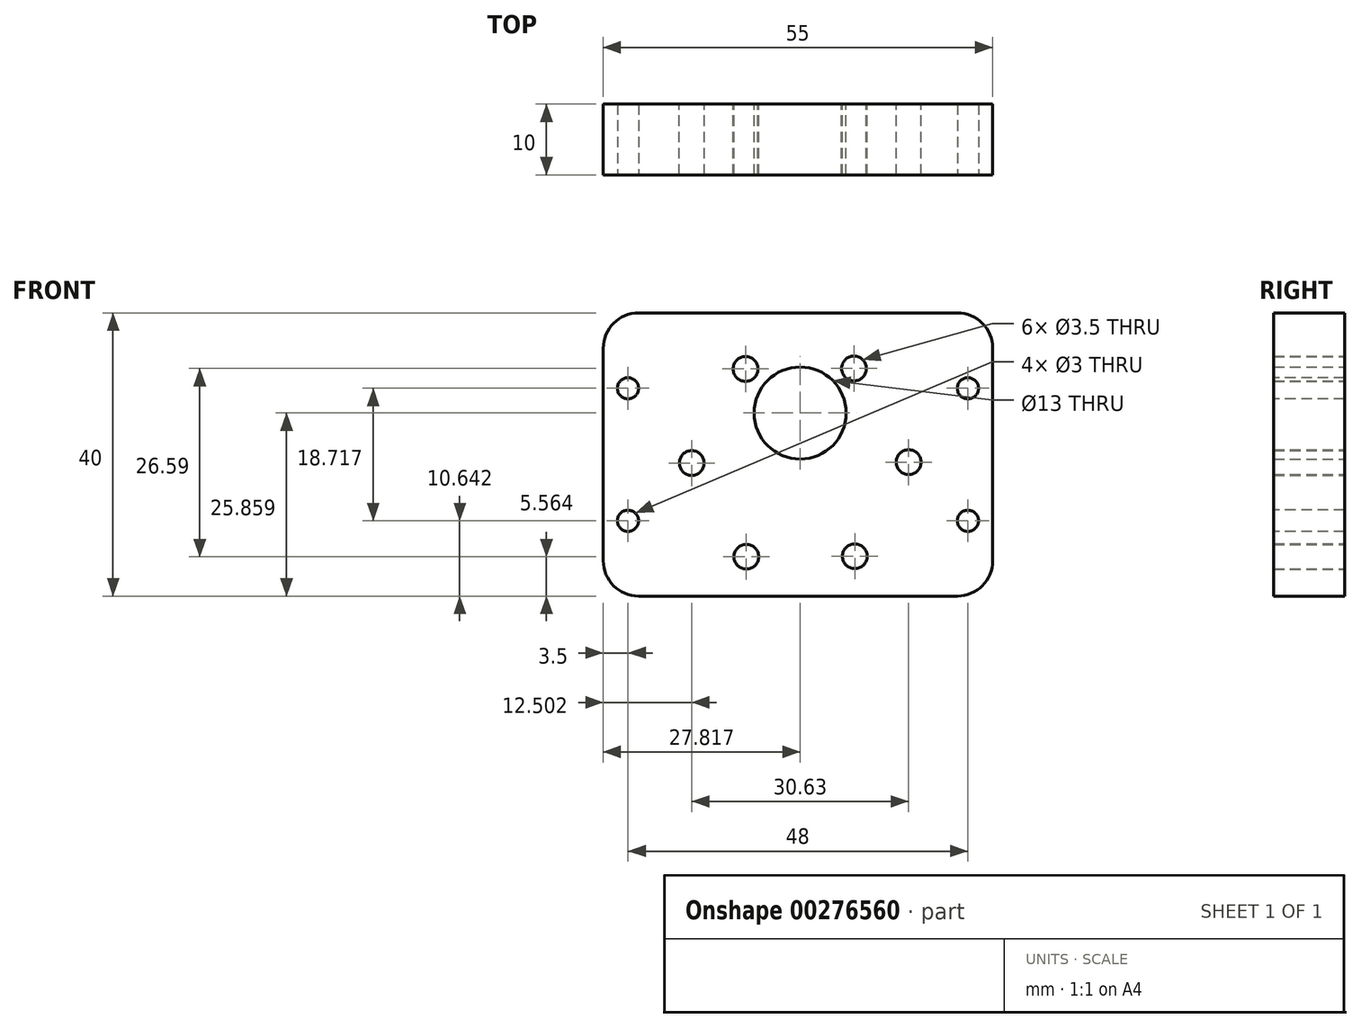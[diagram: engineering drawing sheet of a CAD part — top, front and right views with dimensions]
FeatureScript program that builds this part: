
annotation { "Feature Type Name" : "Feature", "Feature Type Description" : "" }
export const myFeature = defineFeature(function(context is Context, id is Id, definition is map)
    precondition{}
    {
        {
            var Q0;
            Q0=qCreatedBy(makeId("Front.planeOp"),FACE);
            var sketch = newSketch(context, id + "F0", { "sketchPlane" : qUnion([Q0])});
            skLineSegment(sketch, "E0.bottom", {"start": v(27.5, -20) * mm, "end": v(-27.5, -20) * mm});
            skLineSegment(sketch, "E0.top", {"start": v(27.5, 20) * mm, "end": v(-27.5, 20) * mm});
            skLineSegment(sketch, "E0.left", {"start": v(27.5, -20) * mm, "end": v(27.5, 20) * mm});
            skLineSegment(sketch, "E0.right", {"start": v(-27.5, -20) * mm, "end": v(-27.5, 20) * mm});
            skPoint(sketch, "E0.middle", {"position": v(0, 0) * mm});
            skPoint(sketch, "E1.middle", {"position": v(-1.68, 7.36) * mm});
            skCircle(sketch, "E2", {"center": v(-7.4, 12.1) * mm, "radius": 1.75 * mm});
            skCircle(sketch, "E3.1.0", {"center": v(-15, -1.2) * mm, "radius": 1.75 * mm});
            skCircle(sketch, "E3.2.0", {"center": v(-7.28, -14.44) * mm, "radius": 1.75 * mm});
            skCircle(sketch, "E3.3.0", {"center": v(8.03, -14.37) * mm, "radius": 1.75 * mm});
            skCircle(sketch, "E3.4.0", {"center": v(15.63, -1.08) * mm, "radius": 1.75 * mm});
            skCircle(sketch, "E3.5.0", {"center": v(7.92, 12.15) * mm, "radius": 1.75 * mm});
            skPoint(sketch, "E3.center", {"position": v(0.32, -1.14) * mm});
            skLineSegment(sketch, "E4", {"start": v(0.32, -1.14) * mm, "end": v(-15, -1.2) * mm});
            skLineSegment(sketch, "E5", {"start": v(0.32, -1.14) * mm, "end": v(-1.68, 7.36) * mm});
            skCircle(sketch, "E6", {"center": v(0.32, 5.86) * mm, "radius": 6.5 * mm});
            skSolve(sketch);
        }
        {
            var Q0;
            Q0 = qSketchRegion(id + "F0", true);
            extrude(context, id + "F1", {"entities" : qUnion([Q0]), "depth" : 10 * mm, "offsetDistance" : 25 * mm});
        }
        {
            var Q0;
            Q0=makeQuery(id+"F1.opExtrude","SWEPT_EDGE",EDGE,{"disambiguationData":[OSD([sQuery(id+"F0.wireOp",EDGE,"E0.top"),sQuery(id+"F0.wireOp",EDGE,"E0.right")])]});
            var Q1;
            Q1=makeQuery(id+"F1.opExtrude","SWEPT_EDGE",EDGE,{"disambiguationData":[OSD([sQuery(id+"F0.wireOp",EDGE,"E0.bottom"),sQuery(id+"F0.wireOp",EDGE,"E0.right")])]});
            var Q2;
            Q2=makeQuery(id+"F1.opExtrude","SWEPT_EDGE",EDGE,{"disambiguationData":[OSD([sQuery(id+"F0.wireOp",EDGE,"E0.bottom"),sQuery(id+"F0.wireOp",EDGE,"E0.left")])]});
            var Q3;
            Q3=makeQuery(id+"F1.opExtrude","SWEPT_EDGE",EDGE,{"disambiguationData":[OSD([sQuery(id+"F0.wireOp",EDGE,"E0.top"),sQuery(id+"F0.wireOp",EDGE,"E0.left")])]});
            fillet(context, id + "F2", {"entities" : qUnion([Q0, Q1, Q2, Q3]), "tangentPropagation" : true, "radius" : 5 * mm, "defaultsChanged" : false, "vertexSettings" : [], "allowEdgeOverflow" : false});
        }
        {
            var Q0;
            Q0=makeQuery(id+"F1.opExtrude","CAP_FACE",FACE,{"disambiguationData":[OSD([sQuery(id+"F0.wireOp",EDGE,"E0.bottom"),sQuery(id+"F0.wireOp",EDGE,"E0.top"),sQuery(id+"F0.wireOp",EDGE,"E0.left"),sQuery(id+"F0.wireOp",EDGE,"E0.right"),sQuery(id+"F0.wireOp",EDGE,"E2"),sQuery(id+"F0.wireOp",EDGE,"E3.1.0"),sQuery(id+"F0.wireOp",EDGE,"E3.2.0"),sQuery(id+"F0.wireOp",EDGE,"E3.3.0"),sQuery(id+"F0.wireOp",EDGE,"E3.4.0"),sQuery(id+"F0.wireOp",EDGE,"E3.5.0"),sQuery(id+"F0.wireOp",EDGE,"E6")])],"isStart":false});
            var sketch = newSketch(context, id + "F3", { "sketchPlane" : qUnion([Q0])});
            skPoint(sketch, "E7.middle", {"position": v(0, 0) * mm});
            skCircle(sketch, "E8", {"center": v(-24, 9.36) * mm, "radius": 1.5 * mm});
            skCircle(sketch, "E9", {"center": v(-24, -9.36) * mm, "radius": 1.5 * mm});
            skCircle(sketch, "E10", {"center": v(24, 9.36) * mm, "radius": 1.5 * mm});
            skCircle(sketch, "E11", {"center": v(24, -9.36) * mm, "radius": 1.5 * mm});
            skSolve(sketch);
        }
        {
            var Q0;
            Q0 = qSketchRegion(id + "F3", true);
            extrude(context, id + "F4", {"entities" : qUnion([Q0]), "operationType" : NewBodyOperationType.REMOVE, "oppositeDirection" : true, "depth" : 25 * mm, "offsetDistance" : 25 * mm});
        }
    });
